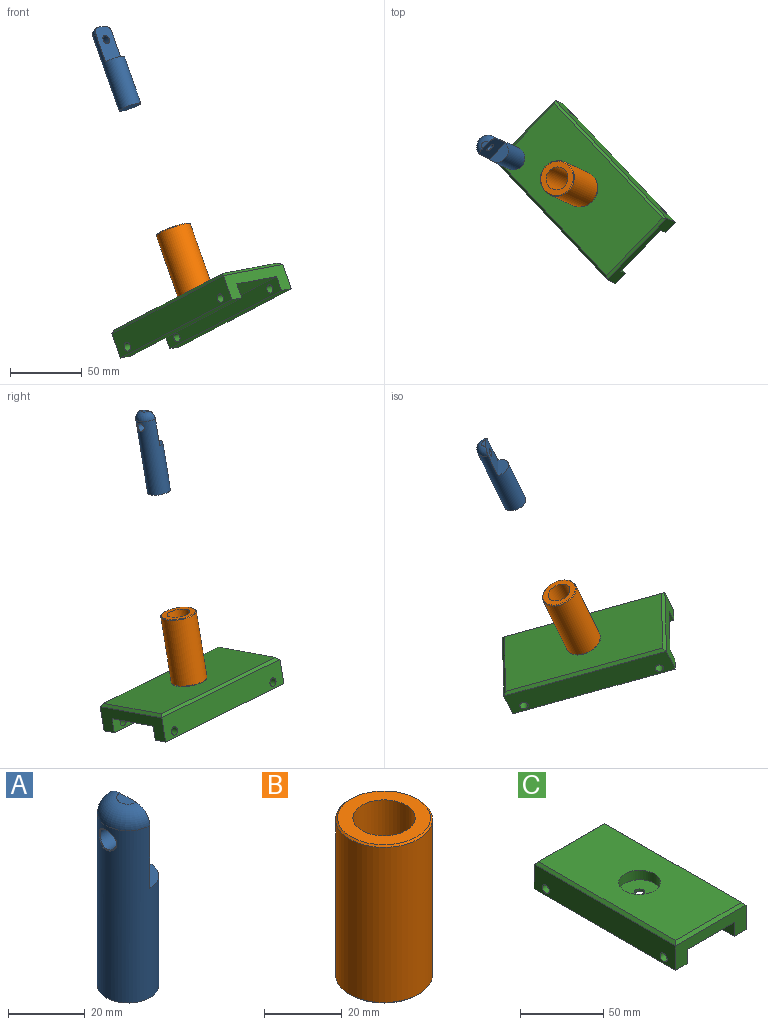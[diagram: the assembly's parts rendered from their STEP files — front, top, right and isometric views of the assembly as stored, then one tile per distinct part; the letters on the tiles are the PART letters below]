
ASSEMBLY  parts=3 mates=2
PART A: 8 faces, bbox 16x16x60 mm
  f0: plane 25x16mm, normal (1,0,0), area 361mm2, adj f1,f2,f4,f5,f7
  f1: cylinder r=8mm len=55mm, axis (0,0,-1), area 2228.2mm2, adj f0,f3,f4,f6,f7
  f2: plane 6x3mm, normal (0,0,1), area 14.1mm2, adj f0,f7
  f3: plane 16x16mm, normal (0,0,-1), area 201.1mm2, adj f1
  f4: plane 16x8mm, normal (0,0,1), area 100.5mm2, adj f0,f1
  f5: cylinder r=3mm len=7.8mm, axis (1,0,0), area 147mm2, adj f0,f6
  f6: bspline ~6.56x6.4mm, area 6.1mm2, adj f1,f5
  f7: torus R=3mm, axis (0,0,1), area 152.6mm2, adj f0,f1,f2
PART B: 8 faces, bbox 25x25x50 mm
  f0: cylinder r=3mm len=6mm, axis (0,0,-1), area 94.2mm2, adj f3,f7
  f1: cylinder r=12.5mm len=49mm, axis (0,0,-1), area 3848.5mm2, adj f4,f5
  f2: plane 24x24mm, normal (0,0,1), area 250.1mm2, adj f4,f6
  f3: plane 24x24mm, normal (0,0,-1), area 424.1mm2, adj f0,f5
  f4: cone r=12mm half-angle=45deg, axis (0,0,-1), area 54.4mm2, adj f1,f2
  f5: cone r=12.5mm half-angle=45deg, axis (0,0,1), area 54.4mm2, adj f1,f3
  f6: cylinder r=8.02mm len=45mm, axis (0,0,1), area 2269mm2, adj f2,f7
  f7: plane 16.05x16.05mm, normal (0,0,1), area 174mm2, adj f0,f6
PART C: 22 faces, bbox 60x120x20 mm
  f0: plane 120x10mm, normal (0,0,-1), area 1200mm2, adj f1,f2,f5,f7
  f1: plane 60x18mm, normal (0,-1,0), area 664.1mm2, adj f0,f3,f4,f5,f7,f8,f9,f17
  f2: plane 60x18mm, normal (0,1,0), area 664.1mm2, adj f0,f3,f4,f5,f7,f8,f9,f20
  f3: plane 120x18mm, normal (-1,0,0), area 2103.5mm2, adj f1,f2,f4,f13,f14,f18
  f4: plane 120x10mm, normal (0,0,-1), area 1200mm2, adj f1,f2,f3,f9
  f5: plane 120x18mm, normal (1,0,0), area 2103.5mm2, adj f0,f1,f2,f15,f16,f19
  f6: plane 116x56mm, normal (0,0,1), area 6005.1mm2, adj f10,f17,f18,f19,f20
  f7: plane 120x10.4mm, normal (-1,0,0), area 1191.3mm2, adj f0,f1,f2,f8,f15,f16
  f8: plane 120x40mm, normal (0,0,-1), area 4749.7mm2, adj f1,f2,f7,f9,f21
  f9: plane 120x10.4mm, normal (1,0,0), area 1191.3mm2, adj f1,f2,f4,f8,f13,f14
  f10: cylinder r=12.5mm len=25mm, axis (0,0,1), area 549.8mm2, adj f6,f11
  f11: plane 25x25mm, normal (0,0,1), area 462.6mm2, adj f10,f12
  f12: cylinder r=3mm len=6mm, axis (0,0,1), area 30.2mm2, adj f11,f21
  f13: cylinder r=3mm len=10mm, axis (1,0,0), area 188.5mm2, adj f3,f9
  f14: cylinder r=3mm len=10mm, axis (1,0,0), area 188.5mm2, adj f3,f9
  f15: cylinder r=3mm len=10mm, axis (1,0,0), area 188.5mm2, adj f5,f7
  f16: cylinder r=3mm len=10mm, axis (1,0,0), area 188.5mm2, adj f5,f7
  f17: plane 60x2mm, normal (0,-0.71,0.71), area 164mm2, adj f1,f6,f18,f19
  f18: plane 120x2mm, normal (-0.71,0,0.71), area 333.8mm2, adj f3,f6,f17,f20
  f19: plane 120x2mm, normal (0.71,0,0.71), area 333.8mm2, adj f5,f6,f17,f20
  f20: plane 60x2mm, normal (0,0.71,0.71), area 164mm2, adj f2,f6,f18,f19
  f21: cone r=3mm half-angle=45deg, axis (0,0,-1), area 31.1mm2, adj f8,f12
PLACE A rot(axis=(-0.01,-0.44,-0.9),49.8deg) t=(-60.68,148.05,132.38)mm
PLACE B rot(axis=(-0.01,-0.44,-0.9),49.8deg) t=(-26.25,187.26,-12.98)mm
PLACE C rot(axis=(0.14,-0.14,-0.98),136.1deg) t=(15.67,144.75,-1.69)mm
MATE slider B.f6 <-> A.f1  axis (-0.33,0.15,0.93) through (-42.7,194.71,33.64)mm
MATE fastened C.f10 <-> B.f1  axis (-0.33,0.15,0.93) through (-26.25,187.26,-12.98)mm
